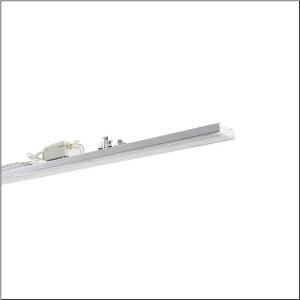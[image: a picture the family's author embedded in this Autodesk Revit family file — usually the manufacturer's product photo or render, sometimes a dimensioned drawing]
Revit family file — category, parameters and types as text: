
# Revit family: licross_11_recessed_ho_51te1emn4d5s
name_source: partatom
category: Lighting Fixtures
units: mm (PartAtom-declared; Revit-internal decimal feet)

## family parameters
Cut with Voids When Loaded = No
Host = Face
Light Source = No
Part Type = Normal
Room Calculation Point = No
Round Connector Dimension = Use Diameter
Shared = No

## types (1)
- --- (1 x LED, 13740 lm, 74.5 W, 4000K)
    Apparent Load = 75 VA
    CIE Flux Codes = 85 95 99 100 100
    Color Rendering = 80
    Color Temperature = 4000K
    Default Elevation = 1800 mm
    Description = Licross 11 Recessed HO, luminaire insert, of sheet steel, galvanised, coil coated, white, length: 1.500mm, width: 66mm, height: 67mm, LED rated luminous flux: 13.740lm, light colour: 840, SDCM (Standard Deviation of Colour Matching)MacAdam ≤ 2 SDCM (initial), control gear: ON/OFF Multilumen, with plug, 3-pole, with phase selection, mains connection: 220..240V, AC, 50/60Hz, rated input power: 75W, internal wiring halogen-free, primary light control with lens, of plastic, primary optical cover: cover, of PMMA, light emission: direct distribution, primary light characteristic: symmetric, protection rating (complete): IP54, insulation class (complete): insulation class I (protective earthing), certification: CE, ENEC, VDE, UKCA, protection symbol: D if used in an environment with non-conductive dust loads with corresponding accessories, impact resistance: IK06, permissible ambient temperature for indoor applications: -35..+35°C, corresponds to IFS (International Featured Standards) requirements for safety and quality in the food industry, reducing of maximum allowable ambient temperature of 5°C with ceiling mounting, The light source and the operating device comply with the requirements of the Ecodesign Regulation (EU) 2019/2020 and are replaceable in accordance with this regulation, packaging unit: 1 piece
    Height = 58 mm
    Lamp = 1 x LED
    Lamp Light Flux = 13740 lm
    Lamp Power = 74.5 W
    Lamp count = 1
    Length = 1500 mm
    Luminous efficacy = 184 lm/W
    Manufacturer = Siteco
    ModVariant = No
    Model = 51TE1EMN4D5S
    Mounting Place = Ceiling
    Mounting Type = Pendant
    Number of Poles = 1
    OnlyDefault = Yes
    Power Factor = 1
    Product Name = Licross 11 Recessed HO
    Product group = luminaire insert | ceiling pendant
    ProductGroupID = 901
    Protection Class = Protection class I
    Protection Degree = IP 54
    RLX_Detail_Level = 1
    RLX_Emergency_Light_Flux = 0 lm
    RLX_Emergency_Type = 0
    RLX_Emergency_Type_DB = No
    RlxData = <blob elided: 22677 chars, md5=558862c2>
    Socket = socket
    Standby Power = 0 W
    System Light Flux = 13740 lm
    System Power = 75 W
    Type Comments = factory setting: luminous flux: 100 % | (A | C | E) | 174 mA
    Type Image = l_1296930.jpg
    URL = http://relux.com
    VarID = @adj_090829
    Voltage = 0 V
    Weight = 0.00 kg
    Width = 66 mm

## geometry (parser evidence)
native form markers: Blend x4, Sweep x12
no freeform markers — native parametric forms only
